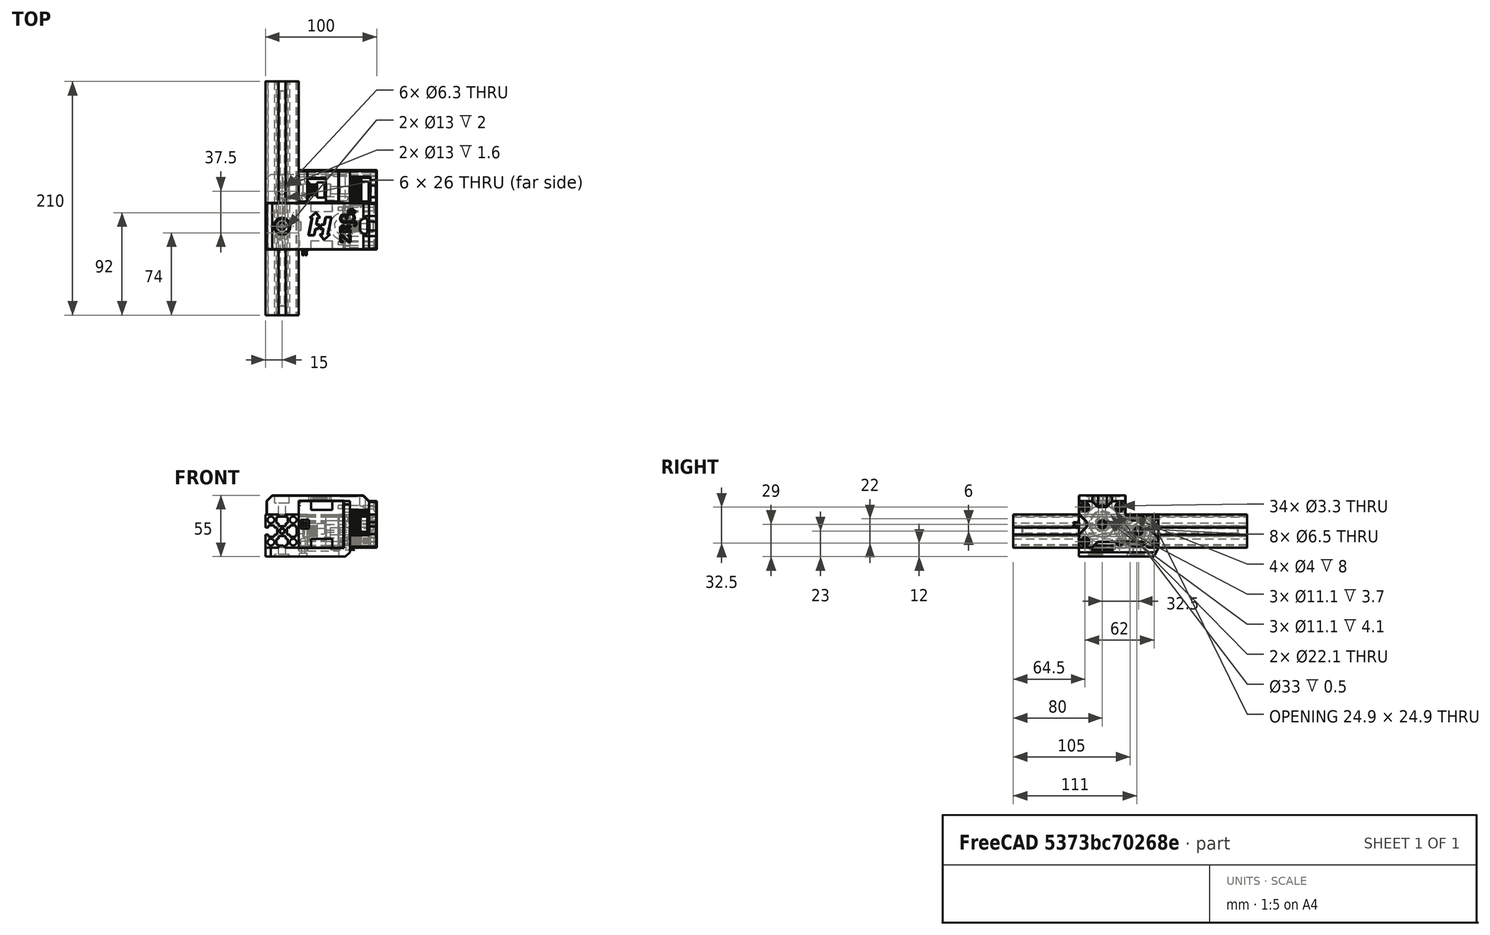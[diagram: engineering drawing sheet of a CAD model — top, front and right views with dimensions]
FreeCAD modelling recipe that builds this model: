
FCSTD DOCUMENT  (FreeCAD 0.18R16146 (Git))
Label: ultra-compact-z-belt
License: All rights reserved
LicenseURL: http://en.wikipedia.org/wiki/All_rights_reserved
objects: Part::Cylinder×51, Part::MultiFuse×38, Part::Chamfer×37, Part::Box×36, Part::Cut×32, Part::Feature×20, Part::Part2DObjectPython×1, Part::Extrusion×1, Part::Torus×1
note: 217 computed .brp shape members not serialized (recipe doc carries the construction recipe); baked Part::Feature solids carry a one-line shape summary decoded from their .brp

FEATURE [Part::Feature] Cut001002  label="40-teeth-pulley"
  Placement = pos=(7,31,15) rot=(0,1,0;1.5708rad)
  shape: bbox 15.7 x 28 x 28 mm, 889 faces (baked)
FEATURE [Part::Feature] Cut001001  label="16-teeth-pulley"
  Placement = pos=(7,0,21) rot=(0,1,0;1.5708rad)
  shape: bbox 14.6 x 13.6 x 13.6 mm, 359 faces (baked)
FEATURE [Part::Feature] Part__Feature032  label="nema17_ldo_cool_power v8"
  Placement = pos=(-39.995,0,21) rot=(0,1,0;1.5708rad)
  shape: bbox 62 x 47 x 42 mm, 103 faces (baked)
FEATURE [Part::Feature] Cut001003  label="16-teeth-pulley001"
  Placement = pos=(-31.5,32.5,15) rot=(0.707107,0,0.707107;3.14159rad)
  shape: bbox 14.6 x 13.6 x 13.6 mm, 359 faces (baked)
FEATURE [Part::Feature] Fusion006002011001  label="210mm-extrusion"
  Placement = pos=(-55,130,15) rot=(1,0,0;1.5708rad)
  shape: bbox 30 x 210 x 30 mm, 69 faces (baked)
FEATURE [Part::Box] Box001  label="Cube001"
  AttacherType = Attacher::AttachEngine3D
  Height = 42
  Length = 6
  Placement = pos=(0,-21,0) rot=(0,0,1;0rad)
  Width = 42
FEATURE [Part::Box] Box002  label="Cube002"
  AttacherType = Attacher::AttachEngine3D
  Height = 30
  Length = 10
  Placement = pos=(-4,21,0) rot=(0,0,1;0rad)
  Width = 29.5
FEATURE [Part::Box] Box003  label="Cube003"
  AttacherType = Attacher::AttachEngine3D
  Height = 8
  Length = 76
  Placement = pos=(-70,-21,-8) rot=(0,0,1;0rad)
  Width = 67.5
FEATURE [Part::Cylinder] Cylinder001
  Angle = 360
  AttacherType = Attacher::AttachEngine3D
  Height = 24
  Placement = pos=(-5e-15,0,21) rot=(0,1,0;1.5708rad)
  Radius = 2.5
FEATURE [Part::MultiFuse] Fusion  label="motor"
  Placement = pos=(0,5e-15,42) rot=(1,0,0;3.14159rad)
  Shapes = -> [Cylinder001,Part__Feature032]
FEATURE [Part::Box] Box004  label="Cube004"
  AttacherType = Attacher::AttachEngine3D
  Height = 30
  Length = 8
  Placement = pos=(-40,21,0) rot=(0,0,1;0rad)
  Width = 29.5
FEATURE [Part::Cylinder] Cylinder
  Angle = 360
  AttacherType = Attacher::AttachEngine3D
  Height = 7
  Placement = pos=(-35,43,15) rot=(0,1,0;1.5708rad)
  Radius = 5
FEATURE [Part::Cylinder] Cylinder002
  Angle = 360
  AttacherType = Attacher::AttachEngine3D
  Height = 25
  Placement = pos=(-40,43,15) rot=(0,1,0;1.5708rad)
  Radius = 2.2
FEATURE [Part::Cylinder] Cylinder005
  Angle = 360
  AttacherType = Attacher::AttachEngine3D
  Height = 4.3
  Placement = pos=(-36.3,31,15) rot=(0,1,0;1.5708rad)
  Radius = 5.55
FEATURE [Part::Cylinder] Cylinder006
  Angle = 360
  AttacherType = Attacher::AttachEngine3D
  Height = 12
  Placement = pos=(-31,31,15) rot=(0,1,0;1.5708rad)
  Radius = 3.25
FEATURE [Part::Box] Box005  label="Cube"
  AttacherType = Attacher::AttachEngine3D
  Height = 3
  Length = 8
  Placement = pos=(-40,46.5,-3) rot=(0,0,1;0rad)
  Width = 4
FEATURE [Part::Box] Box006  label="Cube005"
  AttacherType = Attacher::AttachEngine3D
  Height = 10
  Length = 10
  Placement = pos=(-35,43,10) rot=(0,0,1;0rad)
  Width = 10
FEATURE [Part::Cylinder] Cylinder007
  Angle = 360
  AttacherType = Attacher::AttachEngine3D
  Height = 16
  Placement = pos=(-36,26,-8) rot=(0,0,1;0rad)
  Radius = 1.65
FEATURE [Part::Cylinder] Cylinder008
  Angle = 360
  AttacherType = Attacher::AttachEngine3D
  Height = 16
  Placement = pos=(-36,26,-8) rot=(0,0,1;0rad)
  Radius = 2
FEATURE [Part::Box] Box007  label="Cube006"
  AttacherType = Attacher::AttachEngine3D
  Height = 6
  Length = 3
  Placement = pos=(-42,21,12) rot=(0,0,1;0rad)
  Width = 18
FEATURE [Part::Cylinder] Cylinder014
  Angle = 360
  AttacherType = Attacher::AttachEngine3D
  Height = 9
  Placement = pos=(-31,45,4) rot=(0.57735,-0.57735,0.57735;4.18879rad)
  Radius = 2
FEATURE [Part::Cylinder] Cylinder015
  Angle = 360
  AttacherType = Attacher::AttachEngine3D
  Height = 12
  Placement = pos=(-24,45,26) rot=(0.57735,-0.57735,0.57735;4.18879rad)
  Radius = 1.6
FEATURE [Part::Cylinder] Cylinder011002
  Angle = 360
  AttacherType = Attacher::AttachEngine3D
  Height = 12
  Placement = pos=(-24,45,4) rot=(0.57735,-0.57735,0.57735;4.18879rad)
  Radius = 1.6
FEATURE [Part::MultiFuse] Fusion006002011004003
  Placement = pos=(19,1.5,0) rot=(0,0,1;0rad)
  Shapes = -> [Cylinder015,Cylinder011002]
FEATURE [Part::Box] Box008  label="Cube007"
  AttacherType = Attacher::AttachEngine3D
  Height = 10
  Length = 10
  Placement = pos=(-4,44,-8) rot=(0,0,1;0rad)
  Width = 5
FEATURE [Part::Chamfer] Chamfer002
  Base = -> Box008
  Edges = 1 edges: [Edge11 r1=8 r2=4]
  Placement = pos=(0,1.5,0) rot=(0,0,1;0rad)
FEATURE [Part::Chamfer] Chamfer004
  Base = -> Box001
  Edges = 2 edges r=3: [Edge10,Edge12]
FEATURE [Part::Cylinder] Cylinder011009
  Angle = 360
  AttacherType = Attacher::AttachEngine3D
  Height = 10
  Placement = pos=(13,15.5,5.5) rot=(0,1,0;1.5708rad)
  Radius = 1.65
FEATURE [Part::Cylinder] Cylinder011010
  Angle = 360
  AttacherType = Attacher::AttachEngine3D
  Height = 10
  Placement = pos=(13,-15.5,5.5) rot=(0,1,0;1.5708rad)
  Radius = 1.65
FEATURE [Part::Cylinder] Cylinder011011
  Angle = 360
  AttacherType = Attacher::AttachEngine3D
  Height = 10
  Placement = pos=(13,-15.5,36.5) rot=(0,1,0;1.5708rad)
  Radius = 1.65
FEATURE [Part::Cylinder] Cylinder011012
  Angle = 360
  AttacherType = Attacher::AttachEngine3D
  Height = 10
  Placement = pos=(13,15.5,36.5) rot=(0,1,0;1.5708rad)
  Radius = 1.65
FEATURE [Part::MultiFuse] Fusion006002011004004
  Placement = pos=(-16,0,0) rot=(0,0,1;0rad)
  Shapes = -> [Cylinder011012,Cylinder011011,Cylinder011010,Cylinder011009]
FEATURE [Part::Cut] Cut001014
  Base = -> Chamfer004
  Tool = -> Fusion006002011004004
FEATURE [Part::Box] Box009  label="Cube008"
  AttacherType = Attacher::AttachEngine3D
  Height = 42
  Length = 7
  Placement = pos=(23,-21,0) rot=(0,0,1;0rad)
  Width = 42
FEATURE [Part::Box] Box010  label="Cube009"
  AttacherType = Attacher::AttachEngine3D
  Height = 30
  Length = 5.5
  Placement = pos=(24.5,21,0) rot=(0,0,1;0rad)
  Width = 29.5
FEATURE [Part::Cylinder] Cylinder011013
  Angle = 360
  AttacherType = Attacher::AttachEngine3D
  Height = 10
  Placement = pos=(4,15.5,5.5) rot=(0,1,0;1.5708rad)
  Radius = 3
FEATURE [Part::Cut] Cut001015
  Base = -> Cut001014
  Tool = -> Cylinder011013
FEATURE [Part::Box] Box011  label="Cube010"
  AttacherType = Attacher::AttachEngine3D
  Height = 17
  Length = 29
  Placement = pos=(-69,-21,30) rot=(0,0,1;0rad)
  Width = 42
FEATURE [Part::Box] Box012  label="Cube011"
  AttacherType = Attacher::AttachEngine3D
  Height = 5
  Length = 46
  Placement = pos=(-40,-21,42) rot=(0,0,1;0rad)
  Width = 42
FEATURE [Part::Box] Box013  label="Cube012"
  AttacherType = Attacher::AttachEngine3D
  Height = 15
  Length = 17
  Placement = pos=(6,-21,32) rot=(0,0,1;0rad)
  Width = 42
FEATURE [Part::Cylinder] Cylinder011014
  Angle = 360
  AttacherType = Attacher::AttachEngine3D
  Height = 25
  Placement = pos=(-1,0,21) rot=(0,1,0;1.5708rad)
  Radius = 17
FEATURE [Part::Cylinder] Cylinder011015
  Angle = 360
  AttacherType = Attacher::AttachEngine3D
  Height = 23
  Placement = pos=(-1,0,21) rot=(0,1,0;1.5708rad)
  Radius = 11.05
FEATURE [Part::Cut] Cut001018
  Base = -> Cut001015
  Tool = -> Cylinder011015
FEATURE [Part::Cylinder] Cylinder011016
  Angle = 360
  AttacherType = Attacher::AttachEngine3D
  Height = 17
  Placement = pos=(13,-15.5,36.5) rot=(0,1,0;1.5708rad)
  Radius = 1.65
FEATURE [Part::Cylinder] Cylinder011017
  Angle = 360
  AttacherType = Attacher::AttachEngine3D
  Height = 17
  Placement = pos=(13,15.5,36.5) rot=(0,1,0;1.5708rad)
  Radius = 1.65
FEATURE [Part::MultiFuse] Fusion006002011004007
  Placement = pos=(-7,0,0) rot=(0,0,1;0rad)
  Shapes = -> [Cylinder011017,Cylinder011016]
FEATURE [Part::Cylinder] Cylinder011018
  Angle = 360
  AttacherType = Attacher::AttachEngine3D
  Height = 3
  Placement = pos=(-36,26,-8) rot=(0,0,1;0rad)
  Radius = 3.5
FEATURE [Part::Cylinder] Cylinder011019
  Angle = 360
  AttacherType = Attacher::AttachEngine3D
  Height = 25
  Placement = pos=(-55,0,40) rot=(0,0,1;0rad)
  Radius = 6.5
FEATURE [Part::Cylinder] Cylinder011020
  Angle = 360
  AttacherType = Attacher::AttachEngine3D
  Height = 25
  Placement = pos=(-55,0,26) rot=(0,0,1;0rad)
  Radius = 3.15
FEATURE [Part::Box] Box016  label="Cube015"
  AttacherType = Attacher::AttachEngine3D
  Height = 2
  Length = 6
  Placement = pos=(-58,-21,28) rot=(0,0,1;0rad)
  Width = 17
FEATURE [Part::Box] Box017  label="Cube016"
  AttacherType = Attacher::AttachEngine3D
  Height = 2
  Length = 6
  Placement = pos=(-58,4,28) rot=(0,0,1;0rad)
  Width = 17
FEATURE [Part::Cylinder] Cylinder011021
  Angle = 360
  AttacherType = Attacher::AttachEngine3D
  Height = 10
  Placement = pos=(21,15.5,36.5) rot=(0,1,0;1.5708rad)
  Radius = 3.5
FEATURE [Part::Cylinder] Cylinder011022
  Angle = 360
  AttacherType = Attacher::AttachEngine3D
  Height = 10
  Placement = pos=(21,-15.5,36.5) rot=(0,1,0;1.5708rad)
  Radius = 3.5
FEATURE [Part::Cylinder] Cylinder011023
  Angle = 360
  AttacherType = Attacher::AttachEngine3D
  Height = 10
  Placement = pos=(21,-15.5,36.5) rot=(0,1,0;1.5708rad)
  Radius = 1.65
FEATURE [Part::Cylinder] Cylinder011024
  Angle = 360
  AttacherType = Attacher::AttachEngine3D
  Height = 10
  Placement = pos=(21,15.5,36.5) rot=(0,1,0;1.5708rad)
  Radius = 1.65
FEATURE [Part::Cylinder] Cylinder011025
  Angle = 360
  AttacherType = Attacher::AttachEngine3D
  Height = 10
  Placement = pos=(21,-15.5,5.5) rot=(0,1,0;1.5708rad)
  Radius = 3.5
FEATURE [Part::Box] Box018  label="Cube017"
  AttacherType = Attacher::AttachEngine3D
  Height = 12
  Length = 17
  Placement = pos=(6,-21,0) rot=(0,0,1;0rad)
  Width = 12
FEATURE [Part::Cylinder] Cylinder011027
  Angle = 360
  AttacherType = Attacher::AttachEngine3D
  Height = 31
  Placement = pos=(5,-15.5,5.5) rot=(0,1,0;1.5708rad)
  Radius = 1.65
FEATURE [Part::MultiFuse] Fusion006002011004010
  Shapes = -> [Cylinder011023,Cylinder011027,Cylinder011024]
FEATURE [Part::MultiFuse] Fusion006002011004012
  Placement = pos=(6.5,0,0) rot=(0,0,1;0rad)
  Shapes = -> [Cylinder011025,Cylinder011021,Cylinder011022]
FEATURE [Part::Cylinder] Cylinder011028
  Angle = 360
  AttacherType = Attacher::AttachEngine3D
  Height = 20
  Placement = pos=(-24,45,26) rot=(0,1,0;1.5708rad)
  Radius = 1.65
FEATURE [Part::Cylinder] Cylinder011029
  Angle = 360
  AttacherType = Attacher::AttachEngine3D
  Height = 20
  Placement = pos=(-24,45,4) rot=(0,1,0;1.5708rad)
  Radius = 1.65
FEATURE [Part::MultiFuse] Fusion006002011004013
  Placement = pos=(40,1.5,0) rot=(0,0,1;0rad)
  Shapes = -> [Cylinder011029,Cylinder011028]
FEATURE [Part::Cylinder] Cylinder011032
  Angle = 360
  AttacherType = Attacher::AttachEngine3D
  Height = 4.1
  Placement = pos=(23,0,21) rot=(0,1,0;1.5708rad)
  Radius = 5.55
FEATURE [Part::Cylinder] Cylinder011033
  Angle = 360
  AttacherType = Attacher::AttachEngine3D
  Height = 4.1
  Placement = pos=(24.5,32.5,15) rot=(0,1,0;1.5708rad)
  Radius = 5.55
FEATURE [Part::Cylinder] Cylinder011034
  Angle = 360
  AttacherType = Attacher::AttachEngine3D
  Height = 10
  Placement = pos=(22.5,32.5,15) rot=(0,1,0;1.5708rad)
  Radius = 3.25
FEATURE [Part::Cylinder] Cylinder011035
  Angle = 360
  AttacherType = Attacher::AttachEngine3D
  Height = 10
  Placement = pos=(22.5,0,21) rot=(0,1,0;1.5708rad)
  Radius = 3.25
FEATURE [Part::Cylinder] Cylinder011036
  Angle = 360
  AttacherType = Attacher::AttachEngine3D
  Height = 14
  Placement = pos=(-6.5,32.5,15) rot=(0,1,0;1.5708rad)
  Radius = 3.25
FEATURE [Part::Cylinder] Cylinder011039
  Angle = 360
  AttacherType = Attacher::AttachEngine3D
  Height = 2
  Placement = pos=(-55,-6,-10) rot=(0,0,1;0rad)
  Radius = 6.5
FEATURE [Part::Cylinder] Cylinder011040
  Angle = 360
  AttacherType = Attacher::AttachEngine3D
  Height = 2
  Placement = pos=(-55,31.5,-10) rot=(0,0,1;0rad)
  Radius = 6.5
FEATURE [Part::Cylinder] Cylinder011041
  Angle = 360
  AttacherType = Attacher::AttachEngine3D
  Height = 10
  Placement = pos=(-55,31.5,-10) rot=(0,0,1;0rad)
  Radius = 3.15
FEATURE [Part::Cylinder] Cylinder011042
  Angle = 360
  AttacherType = Attacher::AttachEngine3D
  Height = 10
  Placement = pos=(-55,-6,-10) rot=(0,0,1;0rad)
  Radius = 3.15
FEATURE [Part::Box] Box019  label="Cube018"
  AttacherType = Attacher::AttachEngine3D
  Height = 10
  Length = 10
  Placement = pos=(2,-24,-14) rot=(0,0,1;0rad)
  Width = 82
FEATURE [Part::Chamfer] Chamfer013
  Base = -> Box019
  Edges = 1 edges r=4: [Edge2]
FEATURE [Part::Box] Box020  label="Cube019"
  AttacherType = Attacher::AttachEngine3D
  Height = 12
  Length = 15
  Placement = pos=(21,44,9) rot=(0,0,1;0rad)
  Width = 9
FEATURE [Part::Box] Box021  label="Cube020"
  AttacherType = Attacher::AttachEngine3D
  Height = 18
  Length = 10
  Placement = pos=(21,-24,12) rot=(0,0,1;0rad)
  Width = 10
FEATURE [Part::Box] Box022  label="Cube021"
  AttacherType = Attacher::AttachEngine3D
  Height = 10
  Length = 15
  Placement = pos=(21,-9,-5) rot=(0,0,1;0rad)
  Width = 50.5
FEATURE [Part::Box] Box023  label="Cube022"
  AttacherType = Attacher::AttachEngine3D
  Height = 10
  Length = 15
  Placement = pos=(21,-9,37) rot=(0,0,1;0rad)
  Width = 18
FEATURE [Part::Chamfer] Chamfer016
  Base = -> Box023
  Edges = 2 edges r=5: [Edge9,Edge11]
FEATURE [Part::Chamfer] Chamfer017
  Base = -> Box021
  Edges = 2 edges r=7: [Edge11,Edge12]
FEATURE [Part::Chamfer] Chamfer018
  Base = -> Box020
  Edges = 2 edges r=5: [Edge9,Edge10]
  Placement = pos=(0,1.5,0) rot=(0,0,1;0rad)
FEATURE [Part::Box] Box024  label="Cube023"
  AttacherType = Attacher::AttachEngine3D
  Height = 10
  Length = 18
  Placement = pos=(21,21,25) rot=(0,0,1;0rad)
  Width = 20.5
FEATURE [Part::Box] Box025  label="Cube024"
  AttacherType = Attacher::AttachEngine3D
  Height = 3
  Length = 6
  Placement = pos=(-58,-21,-1) rot=(0,0,1;0rad)
  Width = 10
FEATURE [Part::Box] Box026  label="Cube025"
  AttacherType = Attacher::AttachEngine3D
  Height = 3
  Length = 6
  Placement = pos=(-58,-1,-1) rot=(0,0,1;0rad)
  Width = 26
FEATURE [Part::Box] Box027  label="Cube026"
  AttacherType = Attacher::AttachEngine3D
  Height = 3
  Length = 6
  Placement = pos=(-58,36.5,-1) rot=(0,0,1;0rad)
  Width = 10
FEATURE [Part::Cylinder] Cylinder011043
  Angle = 360
  AttacherType = Attacher::AttachEngine3D
  Height = 9
  Placement = pos=(-31,45,26) rot=(0.57735,-0.57735,0.57735;4.18879rad)
  Radius = 2
FEATURE [Part::MultiFuse] Fusion006002011004034
  Shapes = -> [Cylinder007,Cylinder011018]
FEATURE [Part::Cylinder] Cylinder011044
  Angle = 360
  AttacherType = Attacher::AttachEngine3D
  Height = 4.1
  Placement = pos=(-15.5,32.5,15) rot=(0,1,0;1.5708rad)
  Radius = 5.55
FEATURE [Part::Cylinder] Cylinder011048
  Angle = 360
  AttacherType = Attacher::AttachEngine3D
  Height = 8
  Placement = pos=(-4,25,4) rot=(0,1,0;1.5708rad)
  Radius = 2
FEATURE [Part::Cylinder] Cylinder011049
  Angle = 360
  AttacherType = Attacher::AttachEngine3D
  Height = 8
  Placement = pos=(-4,25,26) rot=(0,1,0;1.5708rad)
  Radius = 2
FEATURE [Part::Cylinder] Cylinder011051
  Angle = 360
  AttacherType = Attacher::AttachEngine3D
  Height = 19
  Placement = pos=(-23,32.5,15) rot=(0,1,0;1.5708rad)
  Radius = 3.25
FEATURE [Part::Cylinder] Cylinder011052
  Angle = 360
  AttacherType = Attacher::AttachEngine3D
  Height = 19
  Placement = pos=(-23,25,26) rot=(0,1,0;1.5708rad)
  Radius = 1.65
FEATURE [Part::Cylinder] Cylinder011053
  Angle = 360
  AttacherType = Attacher::AttachEngine3D
  Height = 19
  Placement = pos=(-23,25,4) rot=(0,1,0;1.5708rad)
  Radius = 1.65
FEATURE [Part::Cylinder] Cylinder011054
  Angle = 360
  AttacherType = Attacher::AttachEngine3D
  Height = 28
  Placement = pos=(-32,46.5,26) rot=(0,1,0;1.5708rad)
  Radius = 1.65
FEATURE [Part::Cylinder] Cylinder011055
  Angle = 360
  AttacherType = Attacher::AttachEngine3D
  Height = 28
  Placement = pos=(-32,46.5,4) rot=(0,1,0;1.5708rad)
  Radius = 1.65
FEATURE [Part::Box] Box029  label="Cube028"
  AttacherType = Attacher::AttachEngine3D
  Height = 12
  Length = 19
  Placement = pos=(-16,67,9) rot=(0,0,1;0rad)
  Width = 28
FEATURE [Part::MultiFuse] Fusion006002011004041
  Shapes = -> [Cylinder011049,Cylinder011048]
FEATURE [Part::MultiFuse] Fusion006002011004043
  Shapes = -> [Box016,Box017]
FEATURE [Part::MultiFuse] Fusion006002011004045
  Shapes = -> [Cylinder011020,Cylinder011019]
FEATURE [Part::Box] Box033  label="Cube032"
  AttacherType = Attacher::AttachEngine3D
  Height = 42.5
  Length = 40.5
  Placement = pos=(-48,-21.25,-0.25) rot=(0,0,1;0rad)
  Width = 42.5
FEATURE [Part::Box] Box035  label="Cube034"
  AttacherType = Attacher::AttachEngine3D
  Height = 42.5
  Length = 40.5
  Placement = pos=(-40,-21.25,-0.25) rot=(0,0,1;0rad)
  Width = 42.5
FEATURE [Part::Box] Box036  label="Cube035"
  AttacherType = Attacher::AttachEngine3D
  Height = 42.5
  Length = 40.5
  Placement = pos=(-40,-21.25,-0.25) rot=(0,0,1;0rad)
  Width = 42.5
FEATURE [Part::Cylinder] Cylinder011058
  Angle = 360
  AttacherType = Attacher::AttachEngine3D
  Height = 18
  Placement = pos=(6,45,4) rot=(0,1,0;1.5708rad)
  Radius = 1.65
FEATURE [Part::Cylinder] Cylinder011061
  Angle = 360
  AttacherType = Attacher::AttachEngine3D
  Height = 18
  Placement = pos=(6,45,26) rot=(0,1,0;1.5708rad)
  Radius = 1.65
FEATURE [Part::Box] Box037  label="Cube036"
  AttacherType = Attacher::AttachEngine3D
  Height = 9
  Length = 18.5
  Placement = pos=(6,43.5,0) rot=(0,0,1;0rad)
  Width = 7
FEATURE [Part::Box] Box038  label="Cube037"
  AttacherType = Attacher::AttachEngine3D
  Height = 9
  Length = 18.5
  Placement = pos=(6,43.5,21) rot=(0,0,1;0rad)
  Width = 7
FEATURE [Part::MultiFuse] Fusion006002011004052
  Placement = pos=(0,1.5,0) rot=(0,0,1;0rad)
  Shapes = -> [Cylinder011058,Cylinder011061]
FEATURE [Part::Cylinder] Cylinder011062
  Angle = 360
  AttacherType = Attacher::AttachEngine3D
  Height = 22
  Placement = pos=(6,32.5,15) rot=(0,1,0;1.5708rad)
  Radius = 15
FEATURE [Part::MultiFuse] Fusion006002011004053002
  Placement = pos=(-9,1.5,0) rot=(0,0,1;0rad)
  Shapes = -> [Cylinder011043,Cylinder014]
FEATURE [Part::Feature] hevort_lite_door_handle_2_001001_solid  label="hevort-logo"
  Placement = pos=(-21,-16,43) rot=(-1,0,0;1.5708rad)
  shape: bbox 26 x 29 x 11.01 mm, 30 faces (baked)
FEATURE [Part::Box] Box039  label="Cube038"
  AttacherType = Attacher::AttachEngine3D
  Height = 32
  Length = 10
  Placement = pos=(15,-9,23) rot=(0,0,1;0rad)
  Width = 18
FEATURE [Part::Chamfer] Chamfer024009
  Base = -> Box039
  Edges = 2 edges r=5: [Edge1,Edge3]
FEATURE [Part::MultiFuse] Fusion006002011004053003
  Placement = pos=(0,1.5,0) rot=(0,0,1;0rad)
  Shapes = -> [Box006,Cylinder002,Cylinder]
FEATURE [Part::Cut] Cut
  Base = -> Box004
  Tool = -> Fusion006002011004053003
FEATURE [Part::Cut] Cut001063008002
  Base = -> Cut
  Tool = -> Fusion006002011004053002
FEATURE [Part::MultiFuse] Fusion006002011004053004
  Shapes = -> [Cut001063008002,Box005]
FEATURE [Part::Cut] Cut001063008003
  Base = -> Fusion006002011004053004
  Tool = -> Cylinder008
FEATURE [Part::MultiFuse] Fusion006002011004053005
  Placement = pos=(0,1.5,0) rot=(0,0,1;0rad)
  Shapes = -> [Cylinder005,Cylinder006]
FEATURE [Part::Chamfer] Chamfer
  Base = -> Box022
  Edges = 2 edges r=5: [Edge10,Edge12]
FEATURE [Part::Chamfer] Chamfer024014
  Base = -> Box024
  Edges = 2 edges r=5: [Edge9,Edge11]
FEATURE [Part::MultiFuse] Fusion006002011004053007
  Shapes = -> [Chamfer017,Chamfer,Chamfer016,Chamfer024014,Chamfer018]
FEATURE [Part::MultiFuse] Fusion006002011004053008
  Shapes = -> [Cylinder011035,Cylinder011034]
FEATURE [Part::Cut] Cut001063008008
  Base = -> Cut001063008003
  Tool = -> Fusion006002011004053005
FEATURE [Part::MultiFuse] Fusion006002011004053014
  Shapes = -> [Box007,Cut001063008008]
FEATURE [Part::MultiFuse] Fusion006002011004053015
  Shapes = -> [Box038,Box037]
FEATURE [Part::Cut] Cut001063008010
  Base = -> Fusion006002011004053015
  Tool = -> Fusion006002011004052
FEATURE [Part::Chamfer] Chamfer024015
  Base = -> Cut001063008010
  Edges = 6 edges r=1: [Edge8,Edge9,Edge11,Edge21,Edge24,Edge26]
FEATURE [Part::Chamfer] Chamfer024016
  Base = -> Box018
  Edges = 1 edges r=5: [Edge12]
FEATURE [Part::Chamfer] Chamfer024017
  Base = -> Chamfer024016
  Edges = 1 edges r=1: [Edge11]
FEATURE [Part::MultiFuse] Fusion006002011004053016
  Shapes = -> [Box009,Box010]
FEATURE [Part::Chamfer] Chamfer024018
  Base = -> Fusion006002011004053016
  Edges = 5 edges r=1: [Edge5,Edge7,Edge8,Edge20,Edge22]
FEATURE [Part::MultiFuse] Fusion006002011004053017
  Shapes = -> [Cylinder011032,Cylinder011033]
FEATURE [Part::Cut] Cut001063008012
  Base = -> Chamfer024018
  Tool = -> Fusion006002011004053007
FEATURE [Part::MultiFuse] Fusion006002011004053019
  Shapes = -> [Fusion006002011004012,Fusion006002011004053008,Fusion006002011004010,Fusion006002011004013,Fusion006002011004053017]
FEATURE [Part::MultiFuse] Fusion006002011004053021
  Shapes = -> [Box002,Chamfer002,Box003,Cut001018]
FEATURE [Part::Chamfer] Chamfer024021
  Base = -> Fusion006002011004053021
  Edges = 1 edges r=1: [Edge7]
FEATURE [Part::Cut] Cut001063008014
  Base = -> Chamfer024021
  Tool = -> Chamfer013
FEATURE [Part::Cut] Cut001063008015
  Base = -> Cut001063008014
  Tool = -> Box035
FEATURE [Part::Cut] Cut001063008016
  Base = -> Cut001063008015
  Tool = -> Cylinder011036
FEATURE [Part::Cut] Cut001063008017
  Base = -> Cut001063008016
  Tool = -> Fusion006002011004003
FEATURE [Part::MultiFuse] Fusion006002011004053022
  Shapes = -> [Box027,Box026,Box025]
FEATURE [Part::Chamfer] Chamfer024022
  Base = -> Fusion006002011004053022
  Edges = 3 edges r=2: [Edge6,Edge18,Edge30]
FEATURE [Part::MultiFuse] Fusion006002011004053023
  Shapes = -> [Cut001063008017,Chamfer024022]
FEATURE [Part::MultiFuse] Fusion006002011004053024
  Placement = pos=(0,0,2) rot=(0,0,1;0rad)
  Shapes = -> [Cylinder011039,Cylinder011040,Cylinder011041,Cylinder011042]
FEATURE [Part::Cut] Cut001063008018
  Base = -> Fusion006002011004053023
  Tool = -> Fusion006002011004053024
FEATURE [Part::Chamfer] Chamfer024023
  Base = -> Cut001063008018
  Edges = 2 edges r=5: [Edge77,Edge85]
FEATURE [Part::Cut] Cut001063008019
  Base = -> Chamfer024023
  Tool = -> Fusion006002011004041
FEATURE [Part::Cut] Cut001063008020
  Base = -> Cut001063008019
  Tool = -> Fusion006002011004034
FEATURE [Part::Box] Box040  label="Cube039"
  AttacherType = Attacher::AttachEngine3D
  Height = 30
  Length = 11.5
  Placement = pos=(-15.5,21.25,0) rot=(0,0,1;0rad)
  Width = 29.25
FEATURE [Part::Box] Box041  label="Cube040"
  AttacherType = Attacher::AttachEngine3D
  Height = 3
  Length = 28
  Placement = pos=(-32,46.5,-3) rot=(0,0,1;0rad)
  Width = 4
FEATURE [Part::MultiFuse] Fusion006002011004053025
  Shapes = -> [Cylinder011052,Cylinder011053]
FEATURE [Part::Cut] Cut001063008021
  Base = -> Box040
  Tool = -> Fusion006002011004053025
FEATURE [Part::Cut] Cut001063008022
  Base = -> Cut001063008021
  Tool = -> Cylinder011051
FEATURE [Part::Cut] Cut001063008023
  Base = -> Cut001063008022
  Tool = -> Cylinder011044
FEATURE [Part::Box] Box042  label="Cube041"
  AttacherType = Attacher::AttachEngine3D
  Height = 8
  Length = 16.5
  Placement = pos=(-32,42.5,0) rot=(0,0,1;0rad)
  Width = 8
FEATURE [Part::Box] Box043  label="Cube042"
  AttacherType = Attacher::AttachEngine3D
  Height = 8
  Length = 16.5
  Placement = pos=(-32,42.5,22) rot=(0,0,1;0rad)
  Width = 8
FEATURE [Part::Chamfer] Chamfer024026
  Base = -> Cut001063008023
  Edges = 3 edges r=1: [Edge8,Edge10,Edge11]
FEATURE [Part::Chamfer] Chamfer024027
  Base = -> Box043
  Edges = 3 edges r=1: [Edge10,Edge11,Edge12]
FEATURE [Part::Chamfer] Chamfer024028
  Base = -> Box042
  Edges = 1 edges r=1: [Edge12]
FEATURE [Part::Chamfer] Chamfer024029
  Base = -> Chamfer024027
  Edges = 1 edges r=2: [Edge10]
FEATURE [Part::Chamfer] Chamfer024030
  Base = -> Chamfer024028
  Edges = 1 edges r=2: [Edge7]
FEATURE [Part::Chamfer] Chamfer024031
  Base = -> Chamfer024030
  Edges = 1 edges r=1: [Edge15]
FEATURE [Part::MultiFuse] Fusion006002011004053027
  Shapes = -> [Chamfer024026,Box041,Chamfer024031,Chamfer024029]
FEATURE [Part::MultiFuse] Fusion006002011004053028
  Shapes = -> [Cylinder011055,Cylinder011054]
FEATURE [Part::Chamfer] Chamfer024034
  Base = -> Box029
  Edges = 2 edges r=5: [Edge9,Edge10]
  Placement = pos=(5,-21.5,0) rot=(0,0,1;0rad)
FEATURE [Part::Feature] Chamfer024034001  label="Chamfer024035"
  Placement = pos=(0,-21.5,0) rot=(0,0,1;0rad)
  shape: bbox 19 x 28 x 12 mm, 8 faces (baked)
FEATURE [Part::Cut] Cut001063008009002
  Base = -> Fusion006002011004053027
  Tool = -> Chamfer024034001
FEATURE [Part::Cut] Cut001063008009003
  Base = -> Cut001063008009002
  Tool = -> Fusion006002011004053028
FEATURE [Part::Chamfer] Chamfer024034002  label="spacer-basic"
  Base = -> Cut001063008009003
  Edges = 1 edges: [Edge17 r1=2.99 r2=1.5]
FEATURE [Part::Cut] Cut001063008009005
  Base = -> Fusion006002011004053014
  Tool = -> Box033
FEATURE [Part::Chamfer] Chamfer024034003
  Base = -> Cut001063008009005
  Edges = 1 edges: [Edge64 r1=2.99 r2=1.5]
FEATURE [Part::Chamfer] Chamfer024034004  label="back-plate-basic"
  Base = -> Chamfer024034003
  Edges = 3 edges r=1: [Edge32,Edge34,Edge36]
FEATURE [Part::Cut] Cut001063008009006  label="main-body-basic"
  Base = -> Cut001063008020
  Tool = -> Chamfer024034
FEATURE [Part::Cut] Cut001063008009007
  Base = -> Chamfer024015
  Tool = -> Cylinder011062
FEATURE [Part::Feature] Cut001063008009006001  label="main-body-basic001"
  shape: bbox 76 x 71.5 x 50 mm, 62 faces (baked)
FEATURE [Part::Feature] Chamfer024034004001  label="back-plate-basic001"
  shape: bbox 10 x 29.25 x 33 mm, 27 faces (baked)
FEATURE [Part::Feature] Chamfer024034002001  label="spacer-basic001"
  shape: bbox 28 x 29.25 x 33 mm, 35 faces (baked)
FEATURE [Part::Chamfer] Chamfer024034004003  label="spacer-exp"
  Base = -> Chamfer024034002001
  Edges = 20 edges r=0.4: [Edge4,Edge7,Edge8,Edge21,Edge44,Edge53,Edge54,Edge57,Edge59,Edge61,Edge63,Edge65,Edge83,Edge87,Edge88,Edge90,Edge91,Edge93,Edge94,Edge95]
FEATURE [Part::Chamfer] Chamfer024034004004  label="back-exp"
  Base = -> Chamfer024034004001
  Edges = 16 edges r=0.4: [Edge2,Edge9,Edge11,Edge13,Edge19,Edge22,Edge26,Edge31,Edge39,Edge46,Edge51,Edge53,Edge54,Edge64,Edge66,Edge68]
FEATURE [Part::Chamfer] Chamfer024034004005
  Base = -> Cut001063008009006001
  Edges = 3 edges r=1: [Edge137,Edge143,Edge148]
FEATURE [Part::Chamfer] Chamfer024034004006  label="main-body-exp"
  Base = -> Chamfer024034004005
  Edges = 10 edges r=0.4: [Edge3,Edge32,Edge33,Edge34,Edge35,Edge36,Edge37,Edge95,Edge96,Edge97]
FEATURE [Part::Chamfer] Chamfer024034004007
  Base = -> Chamfer024017
  Edges = 1 edges r=1: [Edge9]
FEATURE [Part::MultiFuse] Fusion006002011004053029
  Shapes = -> [Chamfer024034004007,Cut001063008009007,Cut001063008012]
FEATURE [Part::Cut] Cut001063008009006002  label="front-basic"
  Base = -> Fusion006002011004053029
  Tool = -> Fusion006002011004053019
FEATURE [Part::Feature] Cut001063008009006002001  label="front-basic001"
  shape: bbox 24 x 71.5 x 42 mm, 67 faces (baked)
FEATURE [Part::Chamfer] Chamfer024034004008  label="front-exp"
  Base = -> Cut001063008009006002001
  Edges = 39 edges r=0.4: [Edge1,Edge5,Edge43,Edge48,Edge50,Edge53,Edge54,Edge57,Edge60,Edge64,Edge66,Edge68,Edge70,Edge71,Edge75,Edge76,Edge81,Edge105,Edge106,Edge109,Edge113,Edge115,Edge116,Edge119,Edge121,Edge124,Edge151,Edge161,Edge163,Edge164,Edge166,Edge167,Edge168,Edge169,Edge170,Edge171,Edge172,Edge173,Edge174]
FEATURE [Part::Part2DObjectPython] ShapeString  # Draft 2D object (typed FeaturePython)
  FontFile = <userpath>/Desktop/Perfect DOS VGA 437.ttf
  Placement = pos=(-107,-14,1) rot=(0,0,1;0rad)
  Size = 20
  String = ZRβ
  Tracking = 0
FEATURE [Part::Extrusion] Extrude
  Base = -> ShapeString
  Dir = (0,0,1)
  DirMode = 2
  FaceMakerClass = Part::FaceMakerBullseye
  LengthFwd = 1
  LengthRev = 0
  Placement = pos=(-7.5,94.5,45) rot=(0,0,1;1.5708rad)
  Solid = false
  Symmetric = false
FEATURE [Part::Feature] Daring_Jofo001001_solid  label="beta15"
  Placement = pos=(-68,75,46) rot=(0,0,1;1.5708rad)
  shape: bbox 15 x 12 x 10 mm, 283 faces (baked)
FEATURE [Part::MultiFuse] Fusion006002011004053030
  Placement = pos=(0,-2,0) rot=(0,0,1;0rad)
  Shapes = -> [Extrude,Daring_Jofo001001_solid]
FEATURE [Part::Feature] Pad001001  label="Pad002"
  Placement = pos=(6,14,46) rot=(0,0,1;1.5708rad)
  shape: bbox 3.5 x 6 x 1 mm, 7 faces (baked)
FEATURE [Part::Feature] Pad001002  label="Pad003"
  Placement = pos=(9,14,46) rot=(0,0,-1;1.5708rad)
  shape: bbox 3.5 x 6 x 1 mm, 7 faces (baked)
FEATURE [Part::MultiFuse] Fusion006002011004053031
  Placement = pos=(0,-1,0) rot=(0,0,1;0rad)
  Shapes = -> [Pad001001,Pad001002]
FEATURE [Part::Feature] Body001002  label="Body003"
  Placement = pos=(6.4,14,46) rot=(0,0,1;1.5708rad)
  shape: bbox 2 x 3 x 1 mm, 5 faces (baked)
FEATURE [Part::Feature] Body001003  label="Body004"
  Placement = pos=(8.6,14,46) rot=(0,0,-1;1.5708rad)
  shape: bbox 2 x 3 x 1 mm, 5 faces (baked)
FEATURE [Part::MultiFuse] Fusion006002011004053032  label="up-down-logo"
  Placement = pos=(0,-1,0) rot=(0,0,1;0rad)
  Shapes = -> [Body001002,Body001003]
FEATURE [Part::MultiFuse] Fusion006002011004053033  label="zr-beta-logo"
  Shapes = -> [Fusion006002011004053030,Fusion006002011004053031]
FEATURE [Part::Cut] Cut001063008009006002002
  Base = -> Box013
  Tool = -> Cylinder011014
FEATURE [Part::Chamfer] Chamfer024034004009
  Base = -> Cut001063008009006002002
  Edges = 1 edges r=5: [Edge8]
FEATURE [Part::Cut] Cut001063008009006002003
  Base = -> Chamfer024034004009
  Tool = -> Chamfer024009
FEATURE [Part::Chamfer] Chamfer024034004010
  Base = -> Cut001063008009006002003
  Edges = 2 edges r=2: [Edge25,Edge32]
FEATURE [Part::Chamfer] Chamfer024034004011
  Base = -> Box011
  Edges = 1 edges r=5: [Edge2]
FEATURE [Part::MultiFuse] Fusion006002011004053034
  Shapes = -> [Chamfer024034004011,Box012,Chamfer024034004010]
FEATURE [Part::Cut] Cut001063008009006002004
  Base = -> Fusion006002011004053034
  Tool = -> Fusion006002011004007
FEATURE [Part::Cut] Cut001063008009006002005
  Base = -> Cut001063008009006002004
  Tool = -> Fusion006002011004045
FEATURE [Part::MultiFuse] Fusion006002011004053035
  Shapes = -> [Fusion006002011004043,Cut001063008009006002005]
FEATURE [Part::Cut] Cut001063008009006002006
  Base = -> Fusion006002011004053035
  Tool = -> Box036
FEATURE [Part::Cut] Cut001063008009006002007
  Base = -> Cut001063008009006002006
  Tool = -> hevort_lite_door_handle_2_001001_solid
FEATURE [Part::Cut] Cut001063008009006002008
  Base = -> Cut001063008009006002007
  Tool = -> Fusion006002011004053033
FEATURE [Part::MultiFuse] Fusion006002011004053036  label="top-basic"
  Shapes = -> [Fusion006002011004053032,Cut001063008009006002008]
FEATURE [Part::Feature] Fusion006002011004053036001  label="top-basic001"
  shape: bbox 92 x 42 x 19 mm, 394 faces (baked)
FEATURE [Part::Chamfer] Chamfer024034004012
  Base = -> Fusion006002011004053036001
  Edges = 1 edges r=1: [Edge36]
FEATURE [Part::Chamfer] Chamfer024034004013  label="top-exp"
  Base = -> Chamfer024034004012
  Edges = 30 edges r=0.4: [Edge8,Edge14,Edge15,Edge16,Edge17,Edge18,Edge19,Edge20,Edge21,Edge22,Edge23,Edge24,Edge25,Edge26,Edge27,Edge28,Edge29,Edge30,Edge31,Edge32,Edge33,Edge34,Edge35,Edge36,Edge357,Edge359,Edge364,Edge365,Edge387,Edge397]
FEATURE [Part::Torus] Torus  label="_61TEETH-belt"
  Angle1 = -180
  Angle2 = 180
  Angle3 = 360
  AttacherType = Attacher::AttachEngine3D
  Radius1 = 10
  Radius2 = 2
FEATURE [Part::Feature] Chamfer024034004004001  label="back-exp001"
  shape: bbox 10 x 29.25 x 33 mm, 43 faces (baked)
FEATURE [Part::Feature] Chamfer024034004003001  label="spacer-exp001"
  shape: bbox 28 x 29.25 x 33 mm, 55 faces (baked)
FEATURE [Part::Feature] Fusion006002011004053036002  label="motor001"
  Placement = pos=(0,5e-15,42) rot=(1,0,0;3.14159rad)
  shape: bbox 64 x 47 x 42 mm, 102 faces (baked)
